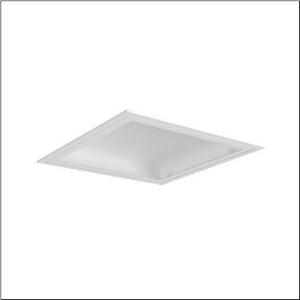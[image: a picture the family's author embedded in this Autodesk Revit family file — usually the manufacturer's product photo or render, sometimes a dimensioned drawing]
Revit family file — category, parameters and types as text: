
# Revit family: mira_21_51fr427a472a
name_source: partatom
category: Lighting Fixtures
units: mm (PartAtom-declared; Revit-internal decimal feet)

## family parameters
Cut with Voids When Loaded = No
Host = Face
Light Source = No
Part Type = Normal
Room Calculation Point = No
Round Connector Dimension = Use Diameter
Shared = No

## types (1)
- Mira 21 (1 x LED, 7680 lm, 66 W, 4000K)
    Apparent Load = 66 VA
    CIE Flux Codes = 50 81 97 100 100
    Color Rendering = 80
    Color Temperature = 4000K
    Default Elevation = 1800 mm
    Description = Mira 21, clean room luminaire, primary light control with reflector, primary optical cover: cover, of PC, light emission: direct distribution, primary light characteristic: symmetric, installation type: recessed, LED, rated luminous flux: 7.680lm, luminous efficacy: 116lm/W, light colour: 840, colour temperature: 4000K, control gear: ON/OFF, with terminal, 3-pole, max. 2.5mm², mains connection: 230V, AC, 50/60Hz, rated input power: 66W, luminaire housing, of sheet steel, coated, pure white (RAL 9010), with concealed spring brackets, module: M625, length: 623mm, width: 623mm, height: 115mm, protection rating (complete): IP54, insulation class (complete): insulation class I (protective earthing), certification: CE, UKCA, permissible operating ambient temperature: -5..+40°C, standard: EN 50419, packaging unit: 1 piece
    Height = 0 mm  [stored 0 ft]
    Lamp = 1 x LED
    Lamp Light Flux = 7680 lm
    Lamp Power = 66 W
    Lamp count = 1
    Length = 625 mm
    Luminous efficacy = 116 lm/W
    Manufacturer = Siteco
    ModVariant = No
    Model = 51FR427A472A
    Mounting Place = Ceiling
    Mounting Type = Recessed
    Number of Poles = 1
    OnlyDefault = Yes
    Power Factor = 1
    Product Name = Mira 21
    Product group = clean room luminaire | ceiling recessed
    ProductGroupID = 402
    Protection Class = Protection class I
    Protection Degree = IP 54
    RLX_Detail_Level = 1
    RLX_Emergency_Light_Flux = 0 lm
    RLX_Emergency_Type = 0
    RLX_Emergency_Type_DB = No
    RlxData = <blob elided: 13377 chars, md5=9088887c>
    Socket = socket
    Standby Power = 0 W
    System Light Flux = 7680 lm
    System Power = 66 W
    Type Comments = Product without accessories
    Type Image = l_1007109.jpg
    URL = http://relux.com
    VarID = ---
    Voltage = 0 V
    Weight = 0.00 kg
    Width = 625 mm

note: [stored X ft] marks values corroborated as IEEE doubles in the binary element streams (Revit-internal decimal feet)

## geometry (parser evidence)
native form markers: Sweep x10
no freeform markers — native parametric forms only
